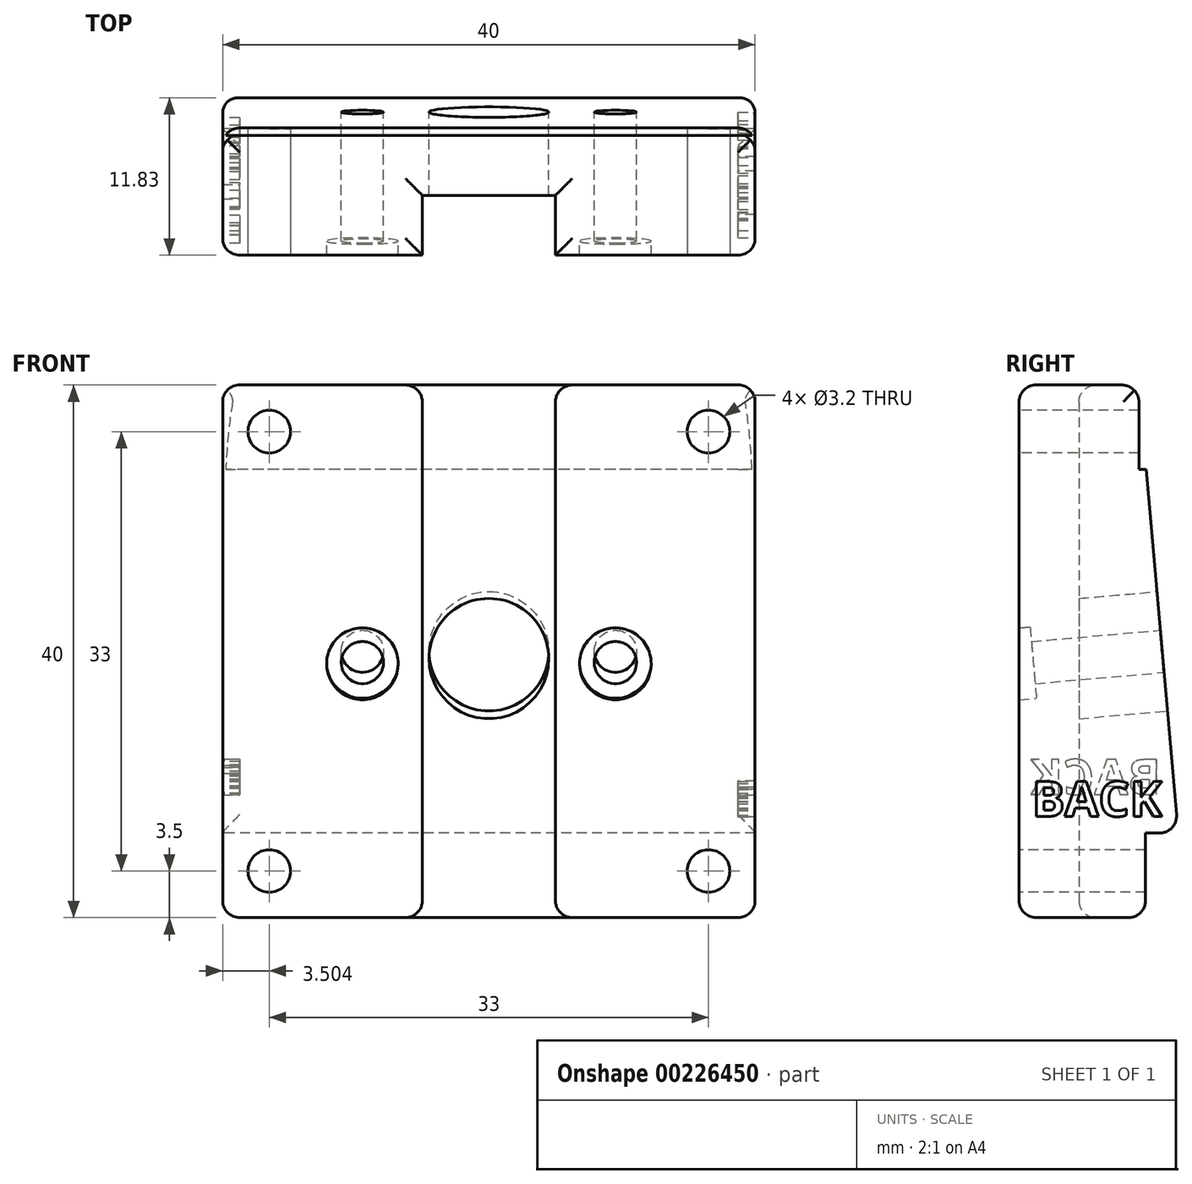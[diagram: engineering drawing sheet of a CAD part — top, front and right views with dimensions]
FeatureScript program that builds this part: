
annotation { "Feature Type Name" : "Feature", "Feature Type Description" : "" }
export const myFeature = defineFeature(function(context is Context, id is Id, definition is map)
    precondition{}
    {
        {
            var Q0;
            Q0=qCreatedBy(makeId("Top.planeOp"),FACE);
            var sketch = newSketch(context, id + "F0", { "sketchPlane" : qUnion([Q0])});
            skLineSegment(sketch, "E0", {"start": v(-39.9, 5.08) * mm, "end": v(-24.9, 5.08) * mm});
            skLineSegment(sketch, "E1", {"start": v(-24.9, 5.08) * mm, "end": v(-24.9, 9.58) * mm});
            skLineSegment(sketch, "E2", {"start": v(-24.9, 9.58) * mm, "end": v(-14.9, 9.58) * mm});
            skLineSegment(sketch, "E3", {"start": v(-14.9, 9.58) * mm, "end": v(-14.9, 5.08) * mm});
            skLineSegment(sketch, "E4", {"start": v(-14.9, 5.08) * mm, "end": v(0.1, 5.08) * mm});
            skLineSegment(sketch, "E5", {"start": v(0.1, 5.08) * mm, "end": v(0.1, 14.08) * mm});
            skLineSegment(sketch, "E6", {"start": v(0.1, 14.08) * mm, "end": v(-39.9, 14.08) * mm});
            skLineSegment(sketch, "E7", {"start": v(-39.9, 14.08) * mm, "end": v(-39.9, 5.08) * mm});
            skSolve(sketch);
        }
        {
            var Q0;
            Q0=makeQuery(id+"F0.imprint","IMPRINT",FACE,{"disambiguationData":[TD([[makeQuery(id+"F0.imprint","IMPRINT",EDGE,{"derivedFrom":sQuery(id+"F0.wireOp",EDGE,"E0")}),1.0]])]});
            extrude(context, id + "F1", {"entities" : qUnion([Q0]), "depth" : 40 * mm});
        }
        {
            var Q0;
            Q0=makeQuery(id+"F1.opExtrude","SWEPT_FACE",FACE,{"disambiguationData":[OSD([sQuery(id+"F0.wireOp",EDGE,"E6")])]});
            var sketch = newSketch(context, id + "F2", { "sketchPlane" : qUnion([Q0])});
            skLineSegment(sketch, "E8", {"start": v(3.4, 36.5) * mm, "end": v(-0.1, 40) * mm});
            skLineSegment(sketch, "E9", {"start": v(36.4, 36.5) * mm, "end": v(39.9, 40) * mm});
            skLineSegment(sketch, "E10", {"start": v(36.4, 3.5) * mm, "end": v(39.9, 0) * mm});
            skLineSegment(sketch, "E11", {"start": v(3.4, 3.5) * mm, "end": v(0, 0) * mm});
            skCircle(sketch, "E12", {"center": v(3.4, 36.5) * mm, "radius": 1.6 * mm});
            skCircle(sketch, "E13", {"center": v(36.4, 36.5) * mm, "radius": 1.6 * mm});
            skCircle(sketch, "E14", {"center": v(36.4, 3.5) * mm, "radius": 1.6 * mm});
            skCircle(sketch, "E15", {"center": v(3.4, 3.5) * mm, "radius": 1.6 * mm});
            skLineSegment(sketch, "E16.bottom", {"start": v(3.4, 36.5) * mm, "end": v(36.4, 36.5) * mm});
            skLineSegment(sketch, "E16.top", {"start": v(3.4, 3.5) * mm, "end": v(36.4, 3.5) * mm});
            skLineSegment(sketch, "E16.left", {"start": v(3.4, 36.5) * mm, "end": v(3.4, 3.5) * mm});
            skLineSegment(sketch, "E16.right", {"start": v(36.4, 36.5) * mm, "end": v(36.4, 3.5) * mm});
            skLineSegment(sketch, "E17.bottom", {"start": v(6.16, 33.75) * mm, "end": v(33.66, 33.75) * mm});
            skLineSegment(sketch, "E17.top", {"start": v(6.16, 6.25) * mm, "end": v(33.66, 6.25) * mm});
            skLineSegment(sketch, "E17.left", {"start": v(6.16, 33.75) * mm, "end": v(6.16, 6.25) * mm});
            skLineSegment(sketch, "E17.right", {"start": v(33.66, 33.75) * mm, "end": v(33.66, 6.25) * mm});
            skLineSegment(sketch, "E18", {"start": v(6.16, 33.75) * mm, "end": v(3.4, 36.5) * mm});
            skLineSegment(sketch, "E19", {"start": v(33.66, 33.75) * mm, "end": v(36.4, 36.5) * mm});
            skLineSegment(sketch, "E20", {"start": v(33.66, 6.25) * mm, "end": v(36.4, 3.5) * mm});
            skLineSegment(sketch, "E21", {"start": v(6.16, 6.25) * mm, "end": v(3.4, 3.5) * mm});
            skLineSegment(sketch, "E22", {"start": v(6.16, 33.75) * mm, "end": v(33.66, 6.25) * mm});
            skLineSegment(sketch, "E23", {"start": v(33.66, 33.75) * mm, "end": v(6.16, 6.25) * mm});
            skCircle(sketch, "E24", {"center": v(19.9, 20) * mm, "radius": 13.75 * mm});
            skLineSegment(sketch, "E25", {"start": v(6.16, 20) * mm, "end": v(33.66, 20) * mm});
            skCircle(sketch, "E26", {"center": v(10.4, 20) * mm, "radius": 1.59 * mm});
            skCircle(sketch, "E27", {"center": v(29.4, 20) * mm, "radius": 1.59 * mm});
            skLineSegment(sketch, "E28", {"start": v(10.4, 20) * mm, "end": v(6.16, 33.75) * mm});
            skLineSegment(sketch, "E29", {"start": v(29.4, 20) * mm, "end": v(33.66, 6.25) * mm});
            skSolve(sketch);
        }
        {
            var Q0;
            Q0=makeQuery(id+"F1.opExtrude","SWEPT_FACE",FACE,{"disambiguationData":[OSD([sQuery(id+"F0.wireOp",EDGE,"E7")])]});
            var sketch = newSketch(context, id + "F3", { "sketchPlane" : qUnion([Q0])});
            skLineSegment(sketch, "E30", {"start": v(-14.08, 0) * mm, "end": v(-17.58, 0) * mm});
            skLineSegment(sketch, "E31", {"start": v(-17.58, 0) * mm, "end": v(-14.08, 40) * mm});
            skLineSegment(sketch, "E32", {"start": v(-17.58, 0) * mm, "end": v(-14.58, 0) * mm});
            skLineSegment(sketch, "E33", {"start": v(-14.58, 0) * mm, "end": v(-14.58, 6.35) * mm});
            skLineSegment(sketch, "E34", {"start": v(-14.58, 6.35) * mm, "end": v(-17.02, 6.35) * mm});
            skLineSegment(sketch, "E35", {"start": v(-14.63, 33.65) * mm, "end": v(-11.63, 33.65) * mm});
            skLineSegment(sketch, "E36", {"start": v(-11.63, 33.65) * mm, "end": v(-11.63, 40) * mm});
            skLineSegment(sketch, "E37", {"start": v(-11.63, 40) * mm, "end": v(-14.08, 40) * mm});
            skLineSegment(sketch, "E38", {"start": v(-8.08, 13.9) * mm, "end": v(-2.8, 13.9) * mm});
            skLineSegment(sketch, "E39", {"start": v(-8.08, 13.9) * mm, "end": v(-7.2, 23.87) * mm});
            skLineSegment(sketch, "E40", {"start": v(-1.92, 23.87) * mm, "end": v(-7.2, 23.87) * mm});
            skLineSegment(sketch, "E41", {"start": v(-9.58, 0) * mm, "end": v(-9.58, 40) * mm});
            skLineSegment(sketch, "E42.MirrorCS", {"start": v(-1.58, 0) * mm, "end": v(-5.08, 40) * mm});
            skLineSegment(sketch, "E43", {"start": v(-1.58, 0) * mm, "end": v(-5.08, 0) * mm});
            skLineSegment(sketch, "E44", {"start": v(-5.08, 0) * mm, "end": v(-5.08, 40) * mm});
            skSolve(sketch);
        }
        {
            var Q0;
            {var subQ0=sQuery(id+"F3.wireOp",EDGE,"E34");var subQ1=sQuery(id+"F3.wireOp",EDGE,"E31");var subQ2=makeQuery(id+"F3.imprint","INTERSECT",VERTEX,{"derivedFrom":[subQ1,subQ0]});Q0=makeQuery(id+"F3.imprint","IMPRINT",FACE,{"disambiguationData":[TD([[makeQuery(id+"F3.imprint","IMPRINT",EDGE,{"disambiguationData":[TD([[subQ2,-1.0]])],"derivedFrom":subQ1}),-1.0]])]});}
            extrude(context, id + "F4", {"entities" : qUnion([Q0]), "operationType" : NewBodyOperationType.ADD, "oppositeDirection" : true, "depth" : 40 * mm, "offsetDistance" : 25.4 * mm});
        }
        {
            var Q0;
            {var subQ1=sQuery(id+"F2.wireOp",EDGE,"E8");var subQ3=sQuery(id+"F2.wireOp",EDGE,"E12");var subQ4=makeQuery(id+"F2.imprint","INTERSECT",VERTEX,{"derivedFrom":[subQ1,subQ3]});Q0=makeQuery(id+"F2.imprint","IMPRINT",FACE,{"disambiguationData":[TD([[makeQuery(id+"F2.imprint","IMPRINT",EDGE,{"disambiguationData":[TD([[subQ4,1.0]])],"derivedFrom":subQ3}),1.0]])]});}
            var Q1;
            {var subQ1=sQuery(id+"F2.wireOp",EDGE,"E8");var subQ3=sQuery(id+"F2.wireOp",EDGE,"E12");var subQ4=makeQuery(id+"F2.imprint","INTERSECT",VERTEX,{"derivedFrom":[subQ1,subQ3]});Q1=makeQuery(id+"F2.imprint","IMPRINT",FACE,{"disambiguationData":[TD([[makeQuery(id+"F2.imprint","IMPRINT",EDGE,{"disambiguationData":[TD([[subQ4,-1.0]])],"derivedFrom":subQ3}),1.0]])]});}
            var Q2;
            {var subQ0=sQuery(id+"F2.wireOp",EDGE,"E16.left");var subQ1=sQuery(id+"F2.wireOp",EDGE,"E12");var subQ2=makeQuery(id+"F2.imprint","INTERSECT",VERTEX,{"derivedFrom":[subQ1,subQ0]});Q2=makeQuery(id+"F2.imprint","IMPRINT",FACE,{"disambiguationData":[TD([[makeQuery(id+"F2.imprint","IMPRINT",EDGE,{"disambiguationData":[TD([[subQ2,-1.0]])],"derivedFrom":subQ1}),1.0]])]});}
            var Q3;
            {var subQ0=sQuery(id+"F2.wireOp",EDGE,"E16.bottom");var subQ1=sQuery(id+"F2.wireOp",EDGE,"E12");var subQ2=makeQuery(id+"F2.imprint","INTERSECT",VERTEX,{"derivedFrom":[subQ1,subQ0]});Q3=makeQuery(id+"F2.imprint","IMPRINT",FACE,{"disambiguationData":[TD([[makeQuery(id+"F2.imprint","IMPRINT",EDGE,{"disambiguationData":[TD([[subQ2,1.0]])],"derivedFrom":subQ1}),1.0]])]});}
            var Q4;
            {var subQ1=sQuery(id+"F2.wireOp",EDGE,"E11");var subQ3=sQuery(id+"F2.wireOp",EDGE,"E15");var subQ4=makeQuery(id+"F2.imprint","INTERSECT",VERTEX,{"derivedFrom":[subQ1,subQ3]});Q4=makeQuery(id+"F2.imprint","IMPRINT",FACE,{"disambiguationData":[TD([[makeQuery(id+"F2.imprint","IMPRINT",EDGE,{"disambiguationData":[TD([[subQ4,-1.0]])],"derivedFrom":subQ3}),1.0]])]});}
            var Q5;
            {var subQ1=sQuery(id+"F2.wireOp",EDGE,"E11");var subQ3=sQuery(id+"F2.wireOp",EDGE,"E15");var subQ4=makeQuery(id+"F2.imprint","INTERSECT",VERTEX,{"derivedFrom":[subQ1,subQ3]});Q5=makeQuery(id+"F2.imprint","IMPRINT",FACE,{"disambiguationData":[TD([[makeQuery(id+"F2.imprint","IMPRINT",EDGE,{"disambiguationData":[TD([[subQ4,1.0]])],"derivedFrom":subQ3}),1.0]])]});}
            var Q6;
            {var subQ0=sQuery(id+"F2.wireOp",EDGE,"E21");var subQ1=sQuery(id+"F2.wireOp",EDGE,"E15");var subQ2=makeQuery(id+"F2.imprint","INTERSECT",VERTEX,{"derivedFrom":[subQ1,subQ0]});Q6=makeQuery(id+"F2.imprint","IMPRINT",FACE,{"disambiguationData":[TD([[makeQuery(id+"F2.imprint","IMPRINT",EDGE,{"disambiguationData":[TD([[subQ2,-1.0]])],"derivedFrom":subQ1}),1.0]])]});}
            var Q7;
            {var subQ0=sQuery(id+"F2.wireOp",EDGE,"E21");var subQ1=sQuery(id+"F2.wireOp",EDGE,"E15");var subQ2=makeQuery(id+"F2.imprint","INTERSECT",VERTEX,{"derivedFrom":[subQ1,subQ0]});Q7=makeQuery(id+"F2.imprint","IMPRINT",FACE,{"disambiguationData":[TD([[makeQuery(id+"F2.imprint","IMPRINT",EDGE,{"disambiguationData":[TD([[subQ2,1.0]])],"derivedFrom":subQ1}),1.0]])]});}
            var Q8;
            {var subQ1=sQuery(id+"F2.wireOp",EDGE,"E10");var subQ3=sQuery(id+"F2.wireOp",EDGE,"E14");var subQ4=makeQuery(id+"F2.imprint","INTERSECT",VERTEX,{"derivedFrom":[subQ1,subQ3]});Q8=makeQuery(id+"F2.imprint","IMPRINT",FACE,{"disambiguationData":[TD([[makeQuery(id+"F2.imprint","IMPRINT",EDGE,{"disambiguationData":[TD([[subQ4,1.0]])],"derivedFrom":subQ3}),1.0]])]});}
            var Q9;
            {var subQ0=sQuery(id+"F2.wireOp",EDGE,"E20");var subQ1=sQuery(id+"F2.wireOp",EDGE,"E14");var subQ2=makeQuery(id+"F2.imprint","INTERSECT",VERTEX,{"derivedFrom":[subQ1,subQ0]});Q9=makeQuery(id+"F2.imprint","IMPRINT",FACE,{"disambiguationData":[TD([[makeQuery(id+"F2.imprint","IMPRINT",EDGE,{"disambiguationData":[TD([[subQ2,-1.0]])],"derivedFrom":subQ1}),1.0]])]});}
            var Q10;
            {var subQ0=sQuery(id+"F2.wireOp",EDGE,"E20");var subQ1=sQuery(id+"F2.wireOp",EDGE,"E14");var subQ2=makeQuery(id+"F2.imprint","INTERSECT",VERTEX,{"derivedFrom":[subQ1,subQ0]});Q10=makeQuery(id+"F2.imprint","IMPRINT",FACE,{"disambiguationData":[TD([[makeQuery(id+"F2.imprint","IMPRINT",EDGE,{"disambiguationData":[TD([[subQ2,1.0]])],"derivedFrom":subQ1}),1.0]])]});}
            var Q11;
            {var subQ1=sQuery(id+"F2.wireOp",EDGE,"E10");var subQ3=sQuery(id+"F2.wireOp",EDGE,"E14");var subQ4=makeQuery(id+"F2.imprint","INTERSECT",VERTEX,{"derivedFrom":[subQ1,subQ3]});Q11=makeQuery(id+"F2.imprint","IMPRINT",FACE,{"disambiguationData":[TD([[makeQuery(id+"F2.imprint","IMPRINT",EDGE,{"disambiguationData":[TD([[subQ4,-1.0]])],"derivedFrom":subQ3}),1.0]])]});}
            var Q12;
            {var subQ1=sQuery(id+"F2.wireOp",EDGE,"E9");var subQ3=sQuery(id+"F2.wireOp",EDGE,"E13");var subQ4=makeQuery(id+"F2.imprint","INTERSECT",VERTEX,{"derivedFrom":[subQ1,subQ3]});Q12=makeQuery(id+"F2.imprint","IMPRINT",FACE,{"disambiguationData":[TD([[makeQuery(id+"F2.imprint","IMPRINT",EDGE,{"disambiguationData":[TD([[subQ4,-1.0]])],"derivedFrom":subQ3}),1.0]])]});}
            var Q13;
            {var subQ0=sQuery(id+"F2.wireOp",EDGE,"E16.bottom");var subQ1=sQuery(id+"F2.wireOp",EDGE,"E13");var subQ2=makeQuery(id+"F2.imprint","INTERSECT",VERTEX,{"derivedFrom":[subQ1,subQ0]});Q13=makeQuery(id+"F2.imprint","IMPRINT",FACE,{"disambiguationData":[TD([[makeQuery(id+"F2.imprint","IMPRINT",EDGE,{"disambiguationData":[TD([[subQ2,-1.0]])],"derivedFrom":subQ1}),1.0]])]});}
            var Q14;
            {var subQ0=sQuery(id+"F2.wireOp",EDGE,"E19");var subQ1=sQuery(id+"F2.wireOp",EDGE,"E13");var subQ2=makeQuery(id+"F2.imprint","INTERSECT",VERTEX,{"derivedFrom":[subQ1,subQ0]});Q14=makeQuery(id+"F2.imprint","IMPRINT",FACE,{"disambiguationData":[TD([[makeQuery(id+"F2.imprint","IMPRINT",EDGE,{"disambiguationData":[TD([[subQ2,-1.0]])],"derivedFrom":subQ1}),1.0]])]});}
            var Q15;
            {var subQ1=sQuery(id+"F2.wireOp",EDGE,"E9");var subQ3=sQuery(id+"F2.wireOp",EDGE,"E13");var subQ4=makeQuery(id+"F2.imprint","INTERSECT",VERTEX,{"derivedFrom":[subQ1,subQ3]});Q15=makeQuery(id+"F2.imprint","IMPRINT",FACE,{"disambiguationData":[TD([[makeQuery(id+"F2.imprint","IMPRINT",EDGE,{"disambiguationData":[TD([[subQ4,1.0]])],"derivedFrom":subQ3}),1.0]])]});}
            extrude(context, id + "F5", {"entities" : qUnion([Q0, Q1, Q2, Q3, Q4, Q5, Q6, Q7, Q8, Q9, Q10, Q11, Q12, Q13, Q14, Q15]), "operationType" : NewBodyOperationType.REMOVE, "depth" : 50.8 * mm, "symmetric" : true});
        }
        {
            var Q0;
            Q0=makeQuery(id+"F4.opExtrude","SWEPT_FACE",FACE,{"disambiguationData":[OSD([sQuery(id+"F3.wireOp",EDGE,"E31")])]});
            var sketch = newSketch(context, id + "F6", { "sketchPlane" : qUnion([Q0])});
            skLineSegment(sketch, "E45.bottom", {"start": v(29.4, 4.84) * mm, "end": v(10.4, 4.84) * mm});
            skLineSegment(sketch, "E45.top", {"start": v(29.4, 32.25) * mm, "end": v(10.4, 32.25) * mm});
            skLineSegment(sketch, "E45.left", {"start": v(29.4, 4.84) * mm, "end": v(29.4, 32.25) * mm});
            skLineSegment(sketch, "E45.right", {"start": v(10.4, 4.84) * mm, "end": v(10.4, 32.25) * mm});
            skLineSegment(sketch, "E46", {"start": v(39.9, 4.84) * mm, "end": v(29.4, 32.25) * mm});
            skLineSegment(sketch, "E47", {"start": v(10.4, 32.25) * mm, "end": v(-0.1, 4.84) * mm});
            skCircle(sketch, "E48", {"center": v(29.4, 18.54) * mm, "radius": 1.59 * mm});
            skCircle(sketch, "E49", {"center": v(10.4, 18.54) * mm, "radius": 1.59 * mm});
            skLineSegment(sketch, "E50", {"start": v(29.4, 18.54) * mm, "end": v(10.4, 18.54) * mm});
            skCircle(sketch, "E51", {"center": v(19.9, 18.54) * mm, "radius": 4.5 * mm});
            skSolve(sketch);
        }
        {
            var Q0;
            {var subQ0=sQuery(id+"F6.wireOp",EDGE,"E48");var subQ1=sQuery(id+"F6.wireOp",EDGE,"E45.left");var subQ2=makeQuery(id+"F6.imprint","INTERSECT",VERTEX,{"disambiguationData":[OD(0.0)],"derivedFrom":[subQ1,subQ0]});Q0=makeQuery(id+"F6.imprint","IMPRINT",FACE,{"disambiguationData":[TD([[makeQuery(id+"F6.imprint","IMPRINT",EDGE,{"disambiguationData":[TD([[subQ2,-1.0]])],"derivedFrom":subQ1}),1.0]])]});}
            var Q1;
            {var subQ0=sQuery(id+"F6.wireOp",EDGE,"E48");var subQ1=sQuery(id+"F6.wireOp",EDGE,"E45.left");var subQ2=makeQuery(id+"F6.imprint","INTERSECT",VERTEX,{"disambiguationData":[OD(0.0)],"derivedFrom":[subQ1,subQ0]});Q1=makeQuery(id+"F6.imprint","IMPRINT",FACE,{"disambiguationData":[TD([[makeQuery(id+"F6.imprint","IMPRINT",EDGE,{"disambiguationData":[TD([[subQ2,-1.0]])],"derivedFrom":subQ1}),-1.0]])]});}
            var Q2;
            {var subQ0=sQuery(id+"F6.wireOp",EDGE,"E49");var subQ1=sQuery(id+"F6.wireOp",EDGE,"E45.right");var subQ2=makeQuery(id+"F6.imprint","INTERSECT",VERTEX,{"disambiguationData":[OD(0.0)],"derivedFrom":[subQ1,subQ0]});Q2=makeQuery(id+"F6.imprint","IMPRINT",FACE,{"disambiguationData":[TD([[makeQuery(id+"F6.imprint","IMPRINT",EDGE,{"disambiguationData":[TD([[subQ2,-1.0]])],"derivedFrom":subQ1}),-1.0]])]});}
            var Q3;
            {var subQ0=sQuery(id+"F6.wireOp",EDGE,"E49");var subQ1=sQuery(id+"F6.wireOp",EDGE,"E45.right");var subQ2=makeQuery(id+"F6.imprint","INTERSECT",VERTEX,{"disambiguationData":[OD(0.0)],"derivedFrom":[subQ1,subQ0]});Q3=makeQuery(id+"F6.imprint","IMPRINT",FACE,{"disambiguationData":[TD([[makeQuery(id+"F6.imprint","IMPRINT",EDGE,{"disambiguationData":[TD([[subQ2,-1.0]])],"derivedFrom":subQ1}),1.0]])]});}
            var Q4;
            {var subQ0=sQuery(id+"F6.wireOp",EDGE,"E50");var subQ1=sQuery(id+"F6.wireOp",EDGE,"E45.left");var subQ2=makeQuery(id+"F6.imprint","INTERSECT",VERTEX,{"derivedFrom":[subQ1,subQ0]});Q4=makeQuery(id+"F6.imprint","IMPRINT",FACE,{"disambiguationData":[TD([[makeQuery(id+"F6.imprint","IMPRINT",EDGE,{"disambiguationData":[TD([[subQ2,-1.0]])],"derivedFrom":subQ1}),1.0]])]});}
            var Q5;
            {var subQ0=sQuery(id+"F6.wireOp",EDGE,"E50");var subQ1=sQuery(id+"F6.wireOp",EDGE,"E45.right");var subQ2=makeQuery(id+"F6.imprint","INTERSECT",VERTEX,{"derivedFrom":[subQ1,subQ0]});Q5=makeQuery(id+"F6.imprint","IMPRINT",FACE,{"disambiguationData":[TD([[makeQuery(id+"F6.imprint","IMPRINT",EDGE,{"disambiguationData":[TD([[subQ2,-1.0]])],"derivedFrom":subQ1}),-1.0]])]});}
            var Q6;
            {var subQ0=sQuery(id+"F6.wireOp",EDGE,"E51");var subQ1=sQuery(id+"F6.wireOp",EDGE,"E50");var subQ2=makeQuery(id+"F6.imprint","INTERSECT",VERTEX,{"disambiguationData":[OD(0.0)],"derivedFrom":[subQ1,subQ0]});Q6=makeQuery(id+"F6.imprint","IMPRINT",FACE,{"disambiguationData":[TD([[makeQuery(id+"F6.imprint","IMPRINT",EDGE,{"disambiguationData":[TD([[subQ2,-1.0]])],"derivedFrom":subQ1}),-1.0]])]});}
            var Q7;
            {var subQ0=sQuery(id+"F6.wireOp",EDGE,"E51");var subQ1=sQuery(id+"F6.wireOp",EDGE,"E50");var subQ2=makeQuery(id+"F6.imprint","INTERSECT",VERTEX,{"disambiguationData":[OD(0.0)],"derivedFrom":[subQ1,subQ0]});Q7=makeQuery(id+"F6.imprint","IMPRINT",FACE,{"disambiguationData":[TD([[makeQuery(id+"F6.imprint","IMPRINT",EDGE,{"disambiguationData":[TD([[subQ2,-1.0]])],"derivedFrom":subQ1}),1.0]])]});}
            extrude(context, id + "F7", {"entities" : qUnion([Q0, Q1, Q2, Q3, Q4, Q5, Q6, Q7]), "operationType" : NewBodyOperationType.REMOVE, "oppositeDirection" : true, "depth" : 25.4 * mm});
        }
        {
            var Q0;
            {var subQ0=sQuery(id+"F3.wireOp",EDGE,"E39");Q0=makeQuery(id+"F3.imprint","IMPRINT",FACE,{"disambiguationData":[TD([[makeQuery(id+"F3.imprint","IMPRINT",EDGE,{"derivedFrom":subQ0}),-1.0]])]});}
            extrude(context, id + "F8", {"entities" : qUnion([Q0]), "operationType" : NewBodyOperationType.ADD, "oppositeDirection" : true, "depth" : 4 * mm, "offsetDistance" : 25.4 * mm});
        }
        {
            var Q0;
            Q0=makeQuery(id+"F4.boolean.opBoolean","MERGE",FACE,{"derivedFrom":[makeQuery(id+"F1.opExtrude","SWEPT_FACE",FACE,{"disambiguationData":[OSD([sQuery(id+"F0.wireOp",EDGE,"E5")])]}),makeQuery(id+"F4.opExtrude","CAP_FACE",FACE,{"disambiguationData":[OSD([sQuery(id+"F0.wireOp",EDGE,"E6"),sQuery(id+"F0.wireOp",EDGE,"E7"),sQuery(id+"F3.wireOp",EDGE,"E30"),sQuery(id+"F3.wireOp",EDGE,"E31"),sQuery(id+"F3.wireOp",EDGE,"E33"),sQuery(id+"F3.wireOp",EDGE,"E34"),sQuery(id+"F3.wireOp",EDGE,"E35")])],"isStart":false})]});
            var sketch = newSketch(context, id + "F9", { "sketchPlane" : qUnion([Q0])});
            skLineSegment(sketch, "E52", {"start": v(5.08, 40) * mm, "end": v(5.08, 0) * mm});
            skSolve(sketch);
        }
        {
            var Q0;
            {var subQ0=sQuery(id+"F0.wireOp",EDGE,"E7");Q0=makeQuery(id+"F8.boolean.opBoolean","MERGE",FACE,{"derivedFrom":[makeQuery(id+"F4.boolean.opBoolean","MERGE",FACE,{"derivedFrom":[makeQuery(id+"F1.opExtrude","SWEPT_FACE",FACE,{"disambiguationData":[OSD([subQ0])]}),makeQuery(id+"F4.opExtrude","CAP_FACE",FACE,{"disambiguationData":[OSD([sQuery(id+"F0.wireOp",EDGE,"E6"),subQ0,sQuery(id+"F3.wireOp",EDGE,"E30"),sQuery(id+"F3.wireOp",EDGE,"E31"),sQuery(id+"F3.wireOp",EDGE,"E33"),sQuery(id+"F3.wireOp",EDGE,"E34"),sQuery(id+"F3.wireOp",EDGE,"E35")])],"isStart":true})]}),makeQuery(id+"F8.opExtrude","CAP_FACE",FACE,{"disambiguationData":[OSD([sQuery(id+"F3.wireOp",EDGE,"E38"),sQuery(id+"F3.wireOp",EDGE,"E39"),sQuery(id+"F3.wireOp",EDGE,"E40"),sQuery(id+"F3.wireOp",EDGE,"E44")])],"isStart":true})]});}
            var sketch = newSketch(context, id + "F10", { "sketchPlane" : qUnion([Q0])});
            skText(sketch, "E53", { "text": "BACK\n", "fontName": "OpenSans-Bold.ttf"});
            const initialGuessF10  = {"E53": [-0.01573, 0.00925, 1, 0, 0.00264]};
            skSetInitialGuess(sketch, initialGuessF10);
            skSolve(sketch);
        }
        {
            var Q0;
            Q0=qSketchRegion(id+"F10",true);
            extrude(context, id + "F11", {"entities" : qUnion([Q0]), "operationType" : NewBodyOperationType.REMOVE, "oppositeDirection" : true, "depth" : 1.27 * mm, "offsetDistance" : 25.4 * mm});
        }
        {
            var Q0;
            Q0=makeQuery(id+"FlwmxsfdiDWVzqx_1.boolean.opBoolean","MERGE",FACE,{"derivedFrom":[makeQuery(id+"F4.boolean.opBoolean","MERGE",FACE,{"derivedFrom":[makeQuery(id+"F1.opExtrude","SWEPT_FACE",FACE,{"disambiguationData":[OSD([sQuery(id+"F0.wireOp",EDGE,"E5")])]}),makeQuery(id+"F4.opExtrude","CAP_FACE",FACE,{"disambiguationData":[OSD([sQuery(id+"F0.wireOp",EDGE,"E6"),sQuery(id+"F0.wireOp",EDGE,"E7"),sQuery(id+"F3.wireOp",EDGE,"E30"),sQuery(id+"F3.wireOp",EDGE,"E31"),sQuery(id+"F3.wireOp",EDGE,"E33"),sQuery(id+"F3.wireOp",EDGE,"E34"),sQuery(id+"F3.wireOp",EDGE,"E35")])],"isStart":false})]}),makeQuery(id+"FlwmxsfdiDWVzqx_1.opExtrude","CAP_FACE",FACE,{"disambiguationData":[OSD([sQuery(id+"F3.wireOp",EDGE,"E38"),sQuery(id+"F3.wireOp",EDGE,"E39"),sQuery(id+"F3.wireOp",EDGE,"E40"),sQuery(id+"F9.wireOp",EDGE,"E52")])],"isStart":true})]});
            var sketch = newSketch(context, id + "F12", { "sketchPlane" : qUnion([Q0])});
            skText(sketch, "E54", { "text": "BACK", "fontName": "OpenSans-Bold.ttf"});
            const initialGuessF12  = {"E54": [0.00605, 0.0076, 1, 0, 0.00264]};
            skSetInitialGuess(sketch, initialGuessF12);
            skSolve(sketch);
        }
        {
            var Q0;
            Q0=qSketchRegion(id+"F12",true);
            extrude(context, id + "F13", {"entities" : qUnion([Q0]), "operationType" : NewBodyOperationType.REMOVE, "oppositeDirection" : true, "depth" : 1.27 * mm, "offsetDistance" : 25.4 * mm});
        }
        {
            var Q0;
            Q0=makeQuery(id+"F1.opExtrude","CAP_FACE",FACE,{"disambiguationData":[OSD([sQuery(id+"F0.wireOp",EDGE,"E0"),sQuery(id+"F0.wireOp",EDGE,"E1"),sQuery(id+"F0.wireOp",EDGE,"E2"),sQuery(id+"F0.wireOp",EDGE,"E3"),sQuery(id+"F0.wireOp",EDGE,"E4"),sQuery(id+"F0.wireOp",EDGE,"E5"),sQuery(id+"F0.wireOp",EDGE,"E6"),sQuery(id+"F0.wireOp",EDGE,"E7")])],"isStart":false});
            var Q1;
            Q1=makeQuery(id+"F4.boolean.opBoolean","MERGE",FACE,{"derivedFrom":[makeQuery(id+"F1.opExtrude","CAP_FACE",FACE,{"disambiguationData":[OSD([sQuery(id+"F0.wireOp",EDGE,"E0"),sQuery(id+"F0.wireOp",EDGE,"E1"),sQuery(id+"F0.wireOp",EDGE,"E2"),sQuery(id+"F0.wireOp",EDGE,"E3"),sQuery(id+"F0.wireOp",EDGE,"E4"),sQuery(id+"F0.wireOp",EDGE,"E5"),sQuery(id+"F0.wireOp",EDGE,"E6"),sQuery(id+"F0.wireOp",EDGE,"E7")])],"isStart":true}),makeQuery(id+"F4.opExtrude","SWEPT_FACE",FACE,{"disambiguationData":[OSD([sQuery(id+"F3.wireOp",EDGE,"E30")])]})]});
            var Q2;
            {var subQ0=sQuery(id+"F3.wireOp",EDGE,"E30");var subQ1=sQuery(id+"F0.wireOp",EDGE,"E7");var subQ10=sQuery(id+"F0.wireOp",EDGE,"E0");var subQ12=makeQuery(id+"F1.opExtrude","SWEPT_EDGE",EDGE,{"disambiguationData":[OSD([subQ10,subQ1])]});Q2=makeQuery(id+"F8.boolean.opBoolean","MERGE",EDGE,{"derivedFrom":[makeQuery(id+"FXXd61Wf1yZkUry_1.boolean.opBoolean","SPLIT",EDGE,{"disambiguationData":[TD([makeQuery(id+"F4.opExtrude","SWEPT_FACE",FACE,{"disambiguationData":[OSD([subQ0])]})])],"derivedFrom":subQ12}),makeQuery(id+"FXXd61Wf1yZkUry_1.boolean.opBoolean","SPLIT",EDGE,{"disambiguationData":[TD([makeQuery(id+"FXXd61Wf1yZkUry_1.opExtrude","SWEPT_FACE",FACE,{"disambiguationData":[OSD([sQuery(id+"F3.wireOp",EDGE,"E40")])]})])],"derivedFrom":subQ12}),makeQuery(id+"F8.opExtrude","CAP_EDGE",EDGE,{"disambiguationData":[OSD([sQuery(id+"F3.wireOp",EDGE,"E44")])],"isStart":true})]});}
            var Q3;
            {var subQ0=sQuery(id+"F3.wireOp",EDGE,"E40");Q3=makeQuery(id+"FXXd61Wf1yZkUry_1.boolean.opBoolean","COPY",EDGE,{"disambiguationData":[topologyDisambiguationEdgeConnected([makeQuery(id+"F1.opExtrude","SWEPT_FACE",FACE,{"disambiguationData":[OSD([sQuery(id+"F0.wireOp",EDGE,"E0")])]})])],"derivedFrom":makeQuery(id+"FXXd61Wf1yZkUry_1.opExtrude","SWEPT_EDGE",EDGE,{"disambiguationData":[OSD([subQ0,sQuery(id+"F3.wireOp",EDGE,"E44")])]})});}
            var Q4;
            Q4=makeQuery(id+"F8.opExtrude","CAP_EDGE",EDGE,{"disambiguationData":[OSD([sQuery(id+"F3.wireOp",EDGE,"E44")])],"isStart":false});
            var Q5;
            {var subQ0=sQuery(id+"F3.wireOp",EDGE,"E38");Q5=makeQuery(id+"FXXd61Wf1yZkUry_1.boolean.opBoolean","COPY",EDGE,{"disambiguationData":[topologyDisambiguationEdgeConnected([makeQuery(id+"F1.opExtrude","SWEPT_FACE",FACE,{"disambiguationData":[OSD([sQuery(id+"F0.wireOp",EDGE,"E0")])]})])],"derivedFrom":makeQuery(id+"FXXd61Wf1yZkUry_1.opExtrude","SWEPT_EDGE",EDGE,{"disambiguationData":[OSD([subQ0,sQuery(id+"F3.wireOp",EDGE,"E44")])]})});}
            var Q6;
            {var subQ0=sQuery(id+"F3.wireOp",EDGE,"E40");Q6=makeQuery(id+"FXXd61Wf1yZkUry_1.boolean.opBoolean","COPY",EDGE,{"disambiguationData":[topologyDisambiguationEdgeConnected([makeQuery(id+"F1.opExtrude","SWEPT_FACE",FACE,{"disambiguationData":[OSD([sQuery(id+"F0.wireOp",EDGE,"E4")])]})])],"derivedFrom":makeQuery(id+"FXXd61Wf1yZkUry_1.opExtrude","SWEPT_EDGE",EDGE,{"disambiguationData":[OSD([subQ0,sQuery(id+"F3.wireOp",EDGE,"E44")])]})});}
            var Q7;
            Q7=makeQuery(id+"FlwmxsfdiDWVzqx_1.opExtrude","CAP_EDGE",EDGE,{"disambiguationData":[OSD([sQuery(id+"F9.wireOp",EDGE,"E52")])],"isStart":false});
            var Q8;
            {var subQ0=sQuery(id+"F3.wireOp",EDGE,"E38");var subQ1=sQuery(id+"F3.wireOp",EDGE,"E39");Q8=makeQuery(id+"FXXd61Wf1yZkUry_1.boolean.opBoolean","COPY",EDGE,{"disambiguationData":[TD([makeQuery(id+"F1.opExtrude","SWEPT_FACE",FACE,{"disambiguationData":[OSD([sQuery(id+"F0.wireOp",EDGE,"E3")])]})])],"derivedFrom":makeQuery(id+"FXXd61Wf1yZkUry_1.opExtrude","SWEPT_EDGE",EDGE,{"disambiguationData":[OSD([subQ0,subQ1])]})});}
            var Q9;
            {var subQ0=sQuery(id+"F0.wireOp",EDGE,"E4");var subQ2=sQuery(id+"F3.wireOp",EDGE,"E30");var subQ6=sQuery(id+"F0.wireOp",EDGE,"E5");var subQ12=makeQuery(id+"F1.opExtrude","SWEPT_EDGE",EDGE,{"disambiguationData":[OSD([subQ0,subQ6])]});Q9=makeQuery(id+"FlwmxsfdiDWVzqx_1.boolean.opBoolean","MERGE",EDGE,{"derivedFrom":[makeQuery(id+"FXXd61Wf1yZkUry_1.boolean.opBoolean","SPLIT",EDGE,{"disambiguationData":[TD([makeQuery(id+"F4.opExtrude","SWEPT_FACE",FACE,{"disambiguationData":[OSD([subQ2])]})])],"derivedFrom":subQ12}),makeQuery(id+"FXXd61Wf1yZkUry_1.boolean.opBoolean","SPLIT",EDGE,{"disambiguationData":[TD([makeQuery(id+"FXXd61Wf1yZkUry_1.opExtrude","SWEPT_FACE",FACE,{"disambiguationData":[OSD([sQuery(id+"F3.wireOp",EDGE,"E40")])]})])],"derivedFrom":subQ12}),makeQuery(id+"FlwmxsfdiDWVzqx_1.opExtrude","CAP_EDGE",EDGE,{"disambiguationData":[OSD([sQuery(id+"F9.wireOp",EDGE,"E52")])],"isStart":true})]});}
            fillet(context, id + "F14", {"entities" : qUnion([Q0, Q1, Q2, Q3, Q4, Q5, Q6, Q7, Q8, Q9]), "radius" : 1.27 * mm, "tangentPropagation" : true, "allowEdgeOverflow" : false});
        }
        {
            var Q0;
            Q0=makeQuery(id+"F4.opExtrude","CAP_EDGE",EDGE,{"disambiguationData":[OSD([sQuery(id+"F3.wireOp",EDGE,"E31")])],"isStart":true});
            var Q1;
            Q1=makeQuery(id+"F4.opExtrude","CAP_EDGE",EDGE,{"disambiguationData":[OSD([sQuery(id+"F3.wireOp",EDGE,"E31")])],"isStart":false});
            var Q2;
            Q2=makeQuery(id+"F4.opExtrude","SWEPT_EDGE",EDGE,{"disambiguationData":[OSD([sQuery(id+"F3.wireOp",EDGE,"E31"),sQuery(id+"F3.wireOp",EDGE,"E34")])]});
            fillet(context, id + "F15", {"entities" : qUnion([Q0, Q1, Q2]), "radius" : 1.27 * mm, "tangentPropagation" : true, "allowEdgeOverflow" : false});
        }
        {
            var Q0;
            Q0=makeQuery(id+"F4.opExtrude","SWEPT_FACE",FACE,{"disambiguationData":[OSD([sQuery(id+"F3.wireOp",EDGE,"E31")])]});
            cPlane(context, id + "F16", {"entities" : qUnion([Q0]), "cplaneType" : CPlaneType.OFFSET, "offset" : 9.72 * mm, "oppositeDirection" : true, "width" : 152.4 * mm, "height" : 152.4 * mm});
        }
        {
            var Q0;
            Q0=qCreatedBy(id+"F16.planeOp",FACE);
            var sketch = newSketch(context, id + "F17", { "sketchPlane" : qUnion([Q0])});
            skCircle(sketch, "E55", {"center": v(29.4, 18.54) * mm, "radius": 2.7 * mm});
            skCircle(sketch, "E56.0", {"center": v(10.4, 18.54) * mm, "radius": 1.59 * mm});
            skCircle(sketch, "E57", {"center": v(10.4, 18.54) * mm, "radius": 2.7 * mm});
            skCircle(sketch, "E58.0", {"center": v(29.4, 18.54) * mm, "radius": 1.59 * mm});
            skSolve(sketch);
        }
        {
            var Q0;
            Q0=makeQuery(id+"F17.imprint","IMPRINT",FACE,{"disambiguationData":[TD([[makeQuery(id+"F17.imprint","IMPRINT",EDGE,{"derivedFrom":sQuery(id+"F17.wireOp",EDGE,"E56.0")}),-1.0]])]});
            var Q1;
            Q1=makeQuery(id+"F17.imprint","IMPRINT",FACE,{"disambiguationData":[TD([[makeQuery(id+"F17.imprint","IMPRINT",EDGE,{"derivedFrom":sQuery(id+"F17.wireOp",EDGE,"E55")}),1.0]])]});
            var Q2;
            Q2=makeQuery(id+"F17.imprint","IMPRINT",FACE,{"disambiguationData":[TD([[makeQuery(id+"F17.imprint","IMPRINT",EDGE,{"derivedFrom":sQuery(id+"F17.wireOp",EDGE,"E56.0")}),1.0]])]});
            var Q3;
            Q3=makeQuery(id+"F17.imprint","IMPRINT",FACE,{"disambiguationData":[TD([[makeQuery(id+"F17.imprint","IMPRINT",EDGE,{"derivedFrom":sQuery(id+"F17.wireOp",EDGE,"E58.0")}),1.0]])]});
            extrude(context, id + "F18", {"entities" : qUnion([Q0, Q1, Q2, Q3]), "operationType" : NewBodyOperationType.REMOVE, "oppositeDirection" : true, "depth" : 25.4 * mm, "offsetDistance" : 25.4 * mm});
        }
    });
